# Revit family: Arris Family
name_source: partatom
category: Furniture
revit_build: Autodesk Revit 2018 (Build: 20170223_1515(x64)
units: mm (PartAtom-declared; Revit-internal decimal feet)

## family parameters
Always vertical = Yes
Cut with Voids When Loaded = No
OmniClass Number = 23.40.20.00
OmniClass Title = General Furniture and Specialties
Room Calculation Point = No
Shared = No
Work Plane-Based = No

## types (5) — shared parameters
Table Top Material = Glass

## per-type parameters (varying)
| type | FurnitureType |
| Lounge Chair (680X770X690X440) (Feather Cushion) | Arris Range Family : Arris Lounge Chair (680X770X690) (Feather Cushion) |
| Sofa (1385X580X690X440) (Feather Cushions) | Arris Range Family : Arris Sofa (1385X580X690) (Feather Cushions) |
| Sofa (1385X580X690X440) (Foam Cushions) | Arris Range Family : Arris Sofa (1385X580X690) (Foam Cushions) |
| Lounge Chair (680X770X690X440) (Foam Cushion) | Arris Range Family : Arris Lounge Chair (680X770X690) (Foam Cushion) |
| Table (900X900X330) | Arris Range Family : Arris Table (900X900X330) |

## geometry (parser evidence)
native form markers: Sweep x52
no freeform markers — native parametric forms only
